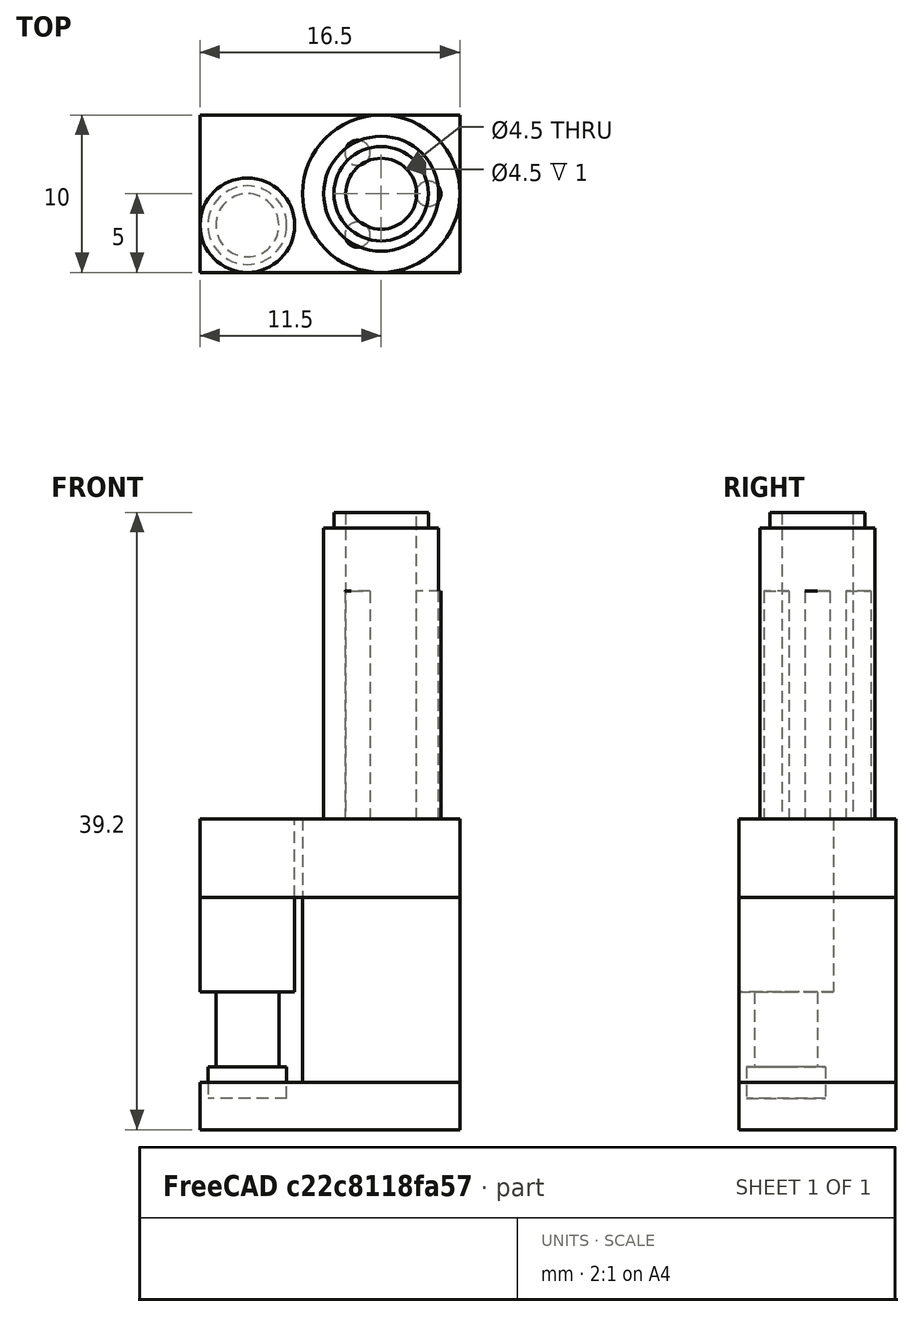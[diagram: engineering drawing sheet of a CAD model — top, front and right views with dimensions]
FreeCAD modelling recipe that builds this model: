
FCSTD DOCUMENT  (FreeCAD 0.20R29603 (Git))
Label: hacklab-fridge-door-post
License: All rights reserved
LicenseURL: http://en.wikipedia.org/wiki/All_rights_reserved
objects: Part::Cylinder×11, Part::Cut×2, Part::Box×2
note: 15 computed .brp shape members not serialized (recipe doc carries the construction recipe); baked Part::Feature solids carry a one-line shape summary decoded from their .brp

FEATURE [Part::Cylinder] Cylinder  label="Bottom (upper)"
  Angle = 360
  AttacherType = Attacher::AttachEngine3D
  FirstAngle = 0
  Height = 11
  Placement = pos=(-8.5,-2,2.25) rot=(0,0,1;0rad)
  Radius = 3
  SecondAngle = 0
FEATURE [Part::Cylinder] Cylinder001  label="Cable tie groove"
  Angle = 360
  AttacherType = Attacher::AttachEngine3D
  FirstAngle = 0
  Height = 4.75
  Placement = pos=(-8.5,-2,-2.5) rot=(0,0,1;0rad)
  Radius = 2
  SecondAngle = 0
FEATURE [Part::Cylinder] Cylinder002  label="Bottom (lower)"
  Angle = 360
  AttacherType = Attacher::AttachEngine3D
  FirstAngle = 0
  Height = 2
  Placement = pos=(-8.5,-2,-4.5) rot=(0,0,1;0rad)
  Radius = 2.5
  SecondAngle = 0
FEATURE [Part::Cylinder] Cylinder003  label="Top (outer 1)"
  Angle = 360
  AttacherType = Attacher::AttachEngine3D
  FirstAngle = 0
  Height = 18.5
  Placement = pos=(0,0,13.2) rot=(0,0,1;0rad)
  Radius = 3.65
  SecondAngle = 0
FEATURE [Part::Cylinder] Cylinder004  label="Top (outer 2)"
  Angle = 360
  AttacherType = Attacher::AttachEngine3D
  FirstAngle = 0
  Height = 1
  Placement = pos=(0,0,31.7) rot=(0,0,1;0rad)
  Radius = 3
  SecondAngle = 0
FEATURE [Part::Cylinder] Cylinder005  label="Top (inner 2)"
  Angle = 360
  AttacherType = Attacher::AttachEngine3D
  FirstAngle = 0
  Height = 1
  Placement = pos=(0,0,31.7) rot=(0,0,1;0rad)
  Radius = 2.25
  SecondAngle = 0
FEATURE [Part::Cylinder] Cylinder006  label="Ridge 0"
  Angle = 360
  AttacherType = Attacher::AttachEngine3D
  FirstAngle = 0
  Height = 14.5
  Placement = pos=(3,0,13.2) rot=(0,0,1;0rad)
  Radius = 0.8
  SecondAngle = 0
FEATURE [Part::Cylinder] Cylinder007  label="Top (inner 1)"
  Angle = 360
  AttacherType = Attacher::AttachEngine3D
  FirstAngle = 0
  Height = 18.5
  Placement = pos=(0,0,13.2) rot=(0,0,1;0rad)
  Radius = 2.25
  SecondAngle = 0
FEATURE [Part::Cut] Cut  label="Top (cut 1)"
  Base = -> Cylinder003
  Tool = -> Cylinder007
FEATURE [Part::Cut] Cut001  label="Top (cut 2)"
  Base = -> Cylinder004
  Tool = -> Cylinder005
FEATURE [Part::Cylinder] Cylinder008  label="Ridge 120"
  Angle = 360
  AttacherType = Attacher::AttachEngine3D
  FirstAngle = 0
  Height = 14.5
  Placement = pos=(-1.5,2.59808,13.2) rot=(0,0,1;2.0944rad)
  Radius = 0.8
  SecondAngle = 0
FEATURE [Part::Cylinder] Cylinder009  label="Ridge 240"
  Angle = 360
  AttacherType = Attacher::AttachEngine3D
  FirstAngle = 0
  Height = 14.5
  Placement = pos=(-1.5,-2.59808,13.2) rot=(0,0,1;4.18879rad)
  Radius = 0.8
  SecondAngle = 0
FEATURE [Part::Box] Box  label="Cube (top)"
  AttacherType = Attacher::AttachEngine3D
  Height = 5
  Length = 16.5
  Placement = pos=(-11.5,-5,8.25) rot=(0,0,1;0rad)
  Width = 10
FEATURE [Part::Cylinder] Cylinder010  label="Bottom (other)"
  Angle = 360
  AttacherType = Attacher::AttachEngine3D
  FirstAngle = 0
  Height = 16.75
  Placement = pos=(0,0,-3.5) rot=(0,0,1;0rad)
  Radius = 5
  SecondAngle = 0
FEATURE [Part::Box] Box001  label="Cube (bottom)"
  AttacherType = Attacher::AttachEngine3D
  Height = 3
  Length = 16.5
  Placement = pos=(-11.5,-5,-6.5) rot=(0,0,1;0rad)
  Width = 10
